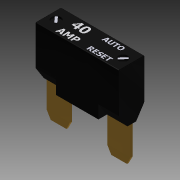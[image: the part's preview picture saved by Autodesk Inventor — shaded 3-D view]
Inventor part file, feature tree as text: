
AUTODESK INVENTOR PART (.ipt)
format: ipt  version: 2014 (Build 180170000, 170)  size: 480,768 bytes
history: native  units: in
note: dims shown in document units (in); Inventor stores cm internally (conversion verified against a paired STEP export)
features: sketch x7, chamfer x6, extrude x5, plane x5, mirror x4, emboss x2, split x1, fillet x1
ambient origin geometry x8: Origin, YZ Plane, XZ Plane, XY Plane, X Axis, Y Axis, Z Axis, Center Point
bodies: Solid1 (feature_tree)
feature tree (31):
  extrude  "Extrusion1"  Depth=0.72in
  extrude  "Extrusion2"  Depth=0.18in
  plane  "Work Plane1"
  mirror  "Mirror1"
  plane  "Work Plane2"
  mirror  "Mirror2"
  extrude  "Extrusion4"  Depth=0.28in TaperAngle=0.0deg
  chamfer  "Chamfer1"  Distance=0.49in
  chamfer  "Chamfer2"  Distance=0.1in Angle=45.0deg
  chamfer  "Chamfer3"  Distance=0.1in Angle=45.0deg
  chamfer  "Chamfer4"  Distance=0.1in Angle=45.0deg
  plane  "Work Plane3"
  mirror  "Mirror3"
  chamfer  "Chamfer5"  Distance=0.1in Angle=45.0deg
  chamfer  "Chamfer6"  Distance=0.05in Angle=45.0deg
  split  "Split1"
  extrude  "Extrusion5"  Depth=0.03in
  plane  "Work Plane4"
  emboss  "Emboss1"
  fillet  "Fillet1"  Radius=0.025in
  plane  "Work Plane5"
  emboss  "Emboss4"
  extrude  "Extrusion7"  Depth=0.03in
  mirror  "Mirror4"
  sketch  "Sketch1"  dims[d0=1.14in d1=0.72in]
  sketch  "Sketch2"  dims[d2=0.35in d3=0.0in d4=0.18in]
  sketch  "Sketch4"  dims[d5=0.1167in d6=0.28in d7=0.0in]
  sketch  "Sketch5"  dims[d13=0.315in]
  sketch  "Sketch6"  dims[d14=0.032in d15=0.49in d16=0.0in d17=0.1in d18=0.05in d19=45.0deg d20=0.1in d21=0.05in d22=45.0deg d23=0.1in d24=0.005in d25=45.0deg d26=0.1in d27=0.005in d28=45.0deg]
  sketch  "Sketch9"  dims[d29=0.0in d30=0.05in d31=0.1in d32=45.0deg]
  sketch  "Sketch10"  dims[d33=0.05in d34=0.1in d35=45.0deg d36=0.125in d37=0.025in d38=0.0in d39=0.1875in d41=0.001in d42=0.0in d43=0.01in d50=0.125in d51=0.0001in d52=0.0in d53=0.03in d56=1.0in d57=0.0in d58=0.456in d59=0.456in]
